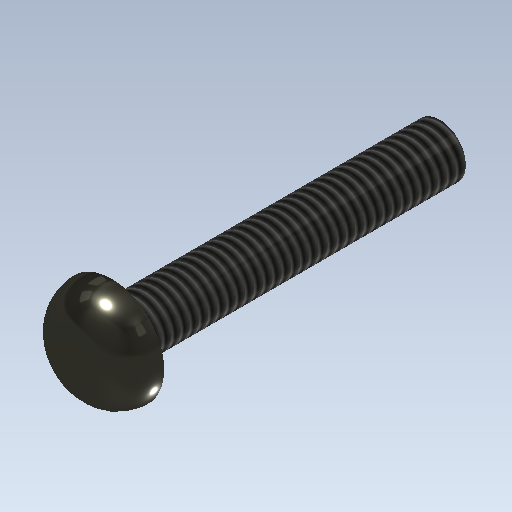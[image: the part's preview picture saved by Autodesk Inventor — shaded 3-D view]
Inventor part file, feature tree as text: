
AUTODESK INVENTOR PART (.ipt)
format: ipt  version: 2020.2 (Build 242310000, 310)  size: 168,960 bytes
history: native  units: mm
features: extrude x3, sketch x3, other x1, fillet x1, thread x1
ambient origin geometry x1: Origin
bodies: Body1 (feature_tree)
feature tree (9):
  other  "ソリッド1"
  extrude  "押し出し1"  Depth=4.0mm
  extrude  "押し出し2"  Depth=6.0mm TaperAngle=0.0deg
  fillet  "フィレット1"  Radius=8.0mm
  thread  "ねじ1"
  extrude  "押し出し3"  Depth=3.0mm TaperAngle=0.0deg
  sketch  "スケッチ1"
  sketch  "スケッチ2"
  sketch  "スケッチ3"
